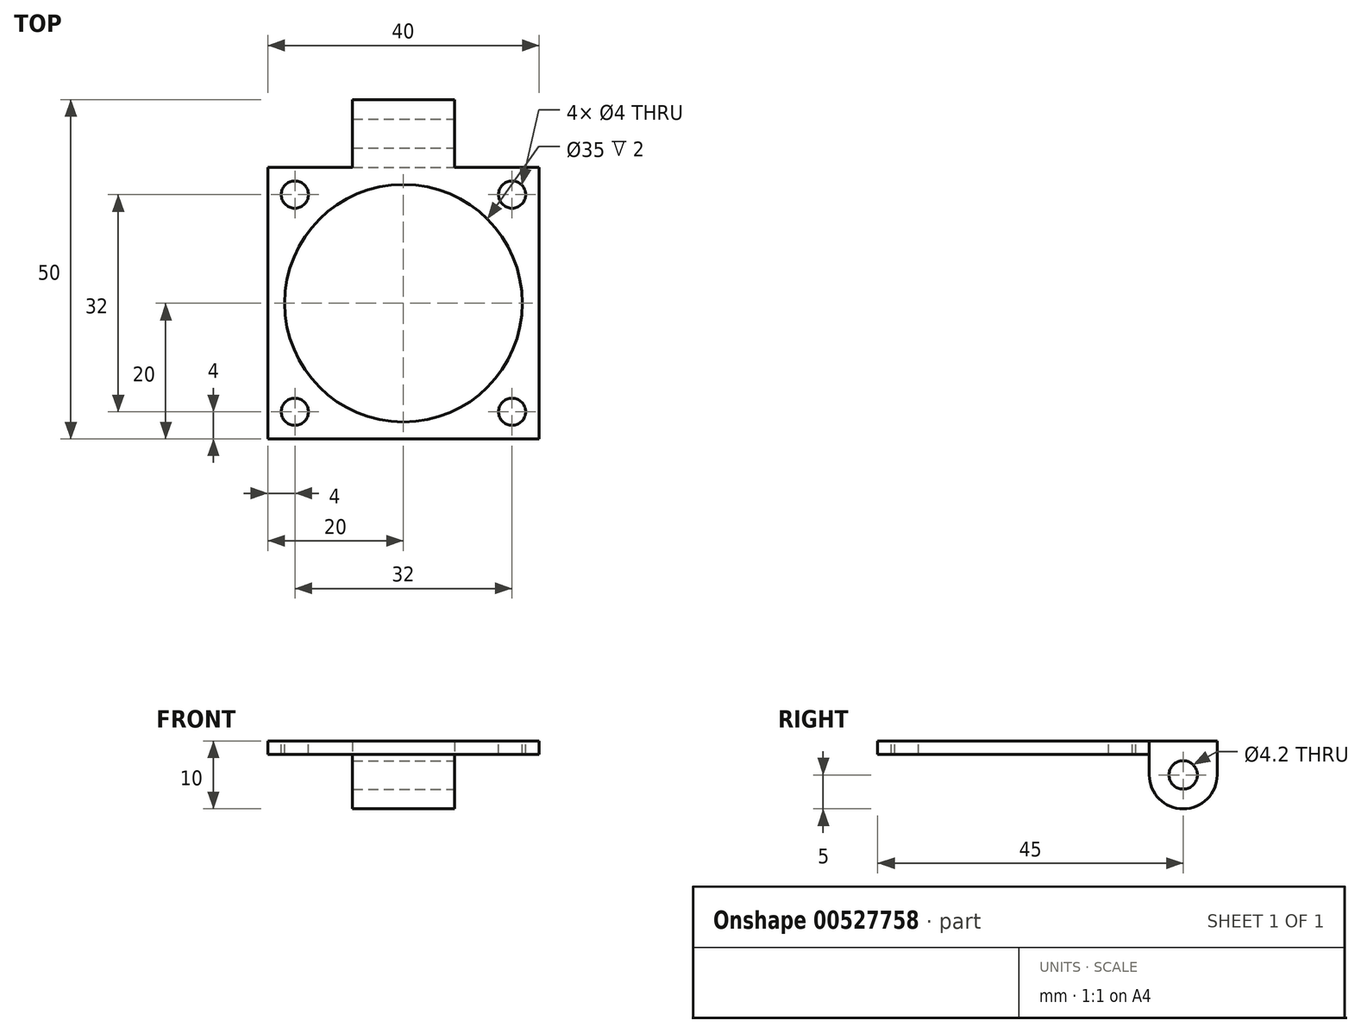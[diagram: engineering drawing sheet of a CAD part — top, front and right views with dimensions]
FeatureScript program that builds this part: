
annotation { "Feature Type Name" : "Feature", "Feature Type Description" : "" }
export const myFeature = defineFeature(function(context is Context, id is Id, definition is map)
    precondition{}
    {
        {
            var Q0;
            Q0=qCreatedBy(makeId("Top.planeOp"),FACE);
            var sketch = newSketch(context, id + "F0", { "sketchPlane" : qUnion([Q0])});
            skLineSegment(sketch, "E0.bottom", {"start": v(0, 0) * mm, "end": v(40, 0) * mm});
            skLineSegment(sketch, "E0.top", {"start": v(0, 40) * mm, "end": v(40, 40) * mm});
            skLineSegment(sketch, "E0.left", {"start": v(0, 0) * mm, "end": v(0, 40) * mm});
            skLineSegment(sketch, "E0.right", {"start": v(40, 0) * mm, "end": v(40, 40) * mm});
            skLineSegment(sketch, "E1", {"start": v(12.5, 40) * mm, "end": v(12.5, 50) * mm});
            skLineSegment(sketch, "E2", {"start": v(12.5, 50) * mm, "end": v(27.5, 50) * mm});
            skLineSegment(sketch, "E3", {"start": v(27.5, 50) * mm, "end": v(27.5, 40) * mm});
            skLineSegment(sketch, "E4", {"start": v(27.5, 40) * mm, "end": v(12.5, 40) * mm});
            skSolve(sketch);
        }
        {
            var Q0;
            Q0 = qSketchRegion(id + "F0", true);
            extrude(context, id + "F1", {"entities" : qUnion([Q0]), "depth" : 2 * mm, "offsetDistance" : 25 * mm});
        }
        {
            var Q0;
            Q0=makeQuery(id+"F1.opExtrude","CAP_FACE",FACE,{"disambiguationData":[OSD([sQuery(id+"F0.wireOp",EDGE,"E0.bottom"),sQuery(id+"F0.wireOp",EDGE,"E0.top"),sQuery(id+"F0.wireOp",EDGE,"E0.left"),sQuery(id+"F0.wireOp",EDGE,"E0.right")])],"isStart":false});
            var sketch = newSketch(context, id + "F2", { "sketchPlane" : qUnion([Q0])});
            skCircle(sketch, "E5", {"center": v(4, 36) * mm, "radius": 2 * mm});
            skCircle(sketch, "E6", {"center": v(36, 36) * mm, "radius": 2 * mm});
            skCircle(sketch, "E7", {"center": v(4, 4) * mm, "radius": 2 * mm});
            skCircle(sketch, "E8", {"center": v(36, 4) * mm, "radius": 2 * mm});
            skSolve(sketch);
        }
        {
            var Q0;
            Q0 = qSketchRegion(id + "F2", true);
            extrude(context, id + "F3", {"entities" : qUnion([Q0]), "operationType" : NewBodyOperationType.REMOVE, "endBound" : BoundingType.THROUGH_ALL, "oppositeDirection" : true, "depth" : 25 * mm, "offsetDistance" : 25 * mm});
        }
        {
            var Q0;
            Q0=makeQuery(id+"F1.opExtrude","CAP_FACE",FACE,{"disambiguationData":[OSD([sQuery(id+"F0.wireOp",EDGE,"E0.bottom"),sQuery(id+"F0.wireOp",EDGE,"E0.top"),sQuery(id+"F0.wireOp",EDGE,"E0.left"),sQuery(id+"F0.wireOp",EDGE,"E0.right")])],"isStart":false});
            var sketch = newSketch(context, id + "F4", { "sketchPlane" : qUnion([Q0])});
            skCircle(sketch, "E9", {"center": v(20, 20) * mm, "radius": 17.5 * mm});
            skSolve(sketch);
        }
        {
            var Q0;
            Q0 = qSketchRegion(id + "F4", true);
            extrude(context, id + "F5", {"entities" : qUnion([Q0]), "operationType" : NewBodyOperationType.REMOVE, "endBound" : BoundingType.THROUGH_ALL, "oppositeDirection" : true, "depth" : 25 * mm, "offsetDistance" : 25 * mm});
        }
        {
            var Q0;
            Q0=makeQuery(id+"F1.opExtrude","CAP_FACE",FACE,{"disambiguationData":[OSD([sQuery(id+"F0.wireOp",EDGE,"E0.bottom"),sQuery(id+"F0.wireOp",EDGE,"E0.top"),sQuery(id+"F0.wireOp",EDGE,"E0.left"),sQuery(id+"F0.wireOp",EDGE,"E0.right"),sQuery(id+"F0.wireOp",EDGE,"E1"),sQuery(id+"F0.wireOp",EDGE,"E2"),sQuery(id+"F0.wireOp",EDGE,"E3")])],"isStart":true});
            var sketch = newSketch(context, id + "F6", { "sketchPlane" : qUnion([Q0])});
            skLineSegment(sketch, "E10.bottom", {"start": v(12.5, -50) * mm, "end": v(27.5, -50) * mm});
            skLineSegment(sketch, "E10.top", {"start": v(12.5, -40) * mm, "end": v(27.5, -40) * mm});
            skLineSegment(sketch, "E10.left", {"start": v(12.5, -50) * mm, "end": v(12.5, -40) * mm});
            skLineSegment(sketch, "E10.right", {"start": v(27.5, -50) * mm, "end": v(27.5, -40) * mm});
            skSolve(sketch);
        }
        {
            var Q0;
            Q0 = qSketchRegion(id + "F6", true);
            extrude(context, id + "F7", {"entities" : qUnion([Q0]), "operationType" : NewBodyOperationType.ADD, "depth" : 8 * mm, "offsetDistance" : 25 * mm});
        }
        {
            var Q0;
            Q0=makeQuery(id+"F7.boolean.opBoolean","MERGE",FACE,{"derivedFrom":[makeQuery(id+"F1.opExtrude","SWEPT_FACE",FACE,{"disambiguationData":[OSD([sQuery(id+"F0.wireOp",EDGE,"E3")])]}),makeQuery(id+"F7.opExtrude","SWEPT_FACE",FACE,{"disambiguationData":[OSD([sQuery(id+"F6.wireOp",EDGE,"E10.right")])]})]});
            var sketch = newSketch(context, id + "F8", { "sketchPlane" : qUnion([Q0])});
            skCircle(sketch, "E11", {"center": v(45, -3) * mm, "radius": 2.1 * mm});
            skSolve(sketch);
        }
        {
            var Q0;
            Q0 = qSketchRegion(id + "F8", true);
            extrude(context, id + "F9", {"entities" : qUnion([Q0]), "operationType" : NewBodyOperationType.REMOVE, "endBound" : BoundingType.THROUGH_ALL, "oppositeDirection" : true, "depth" : 25 * mm, "offsetDistance" : 25 * mm});
        }
        {
            var Q0;
            Q0=makeQuery(id+"F7.opExtrude","CAP_EDGE",EDGE,{"disambiguationData":[OSD([sQuery(id+"F6.wireOp",EDGE,"E10.bottom")])],"isStart":false});
            var Q1;
            Q1=makeQuery(id+"F7.opExtrude","CAP_EDGE",EDGE,{"disambiguationData":[OSD([sQuery(id+"F6.wireOp",EDGE,"E10.top")])],"isStart":false});
            fillet(context, id + "F10", {"entities" : qUnion([Q0, Q1]), "radius" : 5 * mm, "tangentPropagation" : true, "allowEdgeOverflow" : false});
        }
    });
